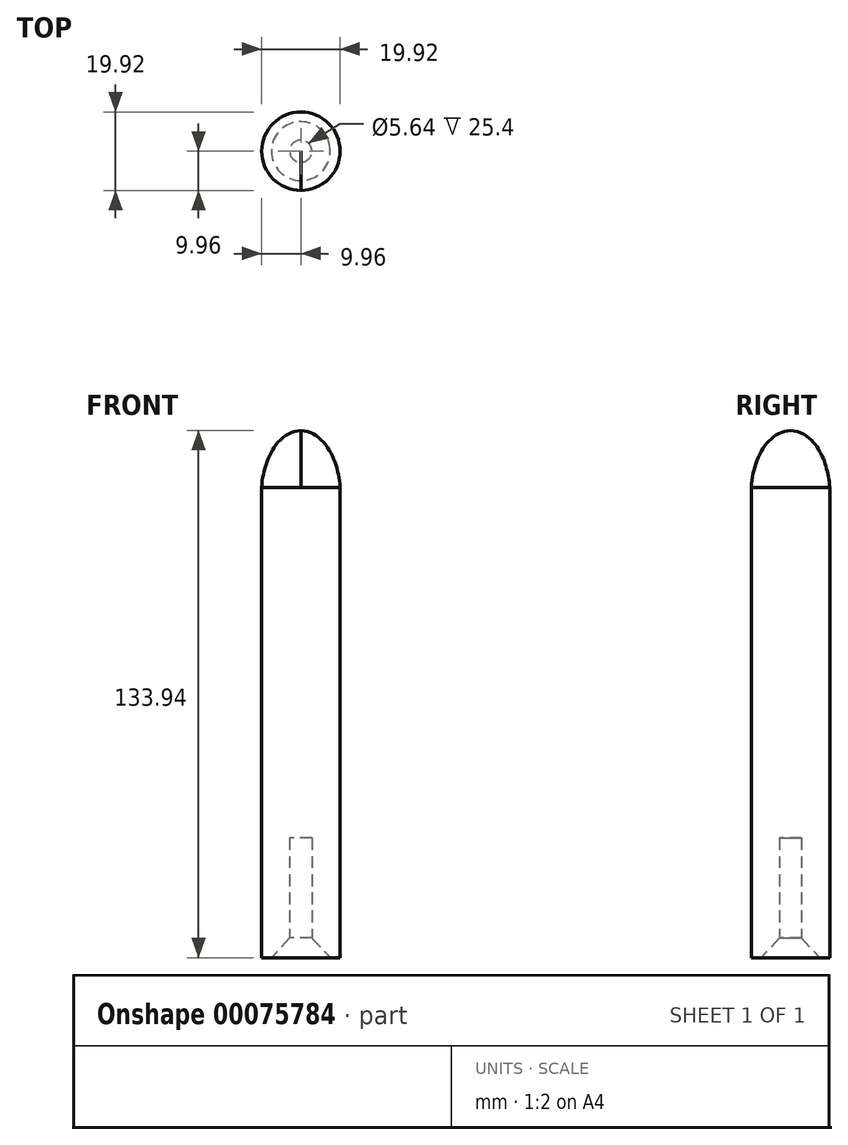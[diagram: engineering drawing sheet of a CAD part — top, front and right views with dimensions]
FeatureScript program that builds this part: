
annotation { "Feature Type Name" : "Feature", "Feature Type Description" : "" }
export const myFeature = defineFeature(function(context is Context, id is Id, definition is map)
    precondition{}
    {
        {
            var Q0;
            Q0=qCreatedBy(makeId("Right.planeOp"),FACE);
            var sketch = newSketch(context, id + "F0", { "sketchPlane" : qUnion([Q0])});
            skLineSegment(sketch, "E0.top", {"start": v(-9.96, -59.73) * mm, "end": v(-7.47, -59.73) * mm});
            skLineSegment(sketch, "E0.left", {"start": v(-9.96, 59.73) * mm, "end": v(-9.96, -59.73) * mm});
            skPoint(sketch, "E0.middle", {"position": v(0, 0) * mm});
            skFitSpline(sketch, "E1", {"points": [v(-9.96, 59.73) * mm, v(0, 74.21) * mm], "startDerivative": vector(1.28, 19.8) * mm, "endDerivative": vector(18.85, 1.28) * mm});
            skLineSegment(sketch, "E2", {"start": v(0, 74.21) * mm, "end": v(0, -54.77) * mm});
            skPoint(sketch, "E0.right.start.orphan", {"position": v(9.96, 59.73) * mm});
            skPoint(sketch, "E3.orphan", {"position": v(9.96, -59.73) * mm});
            skLineSegment(sketch, "E4", {"start": v(-2.82, -54.77) * mm, "end": v(0, -54.77) * mm});
            skPoint(sketch, "E5.orphan", {"position": v(0, -59.73) * mm});
            skLineSegment(sketch, "E6", {"start": v(-2.82, -54.77) * mm, "end": v(-7.47, -59.73) * mm});
            skPoint(sketch, "E7.orphan", {"position": v(-4.98, -59.73) * mm});
            skSolve(sketch);
        }
        {
            var Q0;
            Q0=makeQuery(id+"F0.imprint","IMPRINT",FACE,{"disambiguationData":[TD([[makeQuery(id+"F0.imprint","IMPRINT",EDGE,{"derivedFrom":sQuery(id+"F0.wireOp",EDGE,"E0.top")}),1.0]])]});
            var Q1;
            Q1=sQuery(id+"F0.wireOp",EDGE,"E2");
            revolve(context, id + "F1", {"entities" : qUnion([Q0]), "axis" : qUnion([Q1]), "revolveType" : RevolveType.FULL});
        }
        {
            var Q0;
            Q0=makeQuery(id+"F1.opRevolve","SWEPT_FACE",FACE,{"disambiguationData":[OSD([sQuery(id+"F0.wireOp",EDGE,"E4")])]});
            var sketch = newSketch(context, id + "F2", { "sketchPlane" : qUnion([Q0])});
            skCircle(sketch, "E8.0.0", {"center": v(0, 0) * mm, "radius": 2.82 * mm});
            skSolve(sketch);
        }
        {
            var Q0;
            Q0 = qSketchRegion(id + "F2", true);
            extrude(context, id + "F3", {"entities" : qUnion([Q0]), "operationType" : NewBodyOperationType.REMOVE, "oppositeDirection" : true, "depth" : 25.4 * mm});
        }
    });
